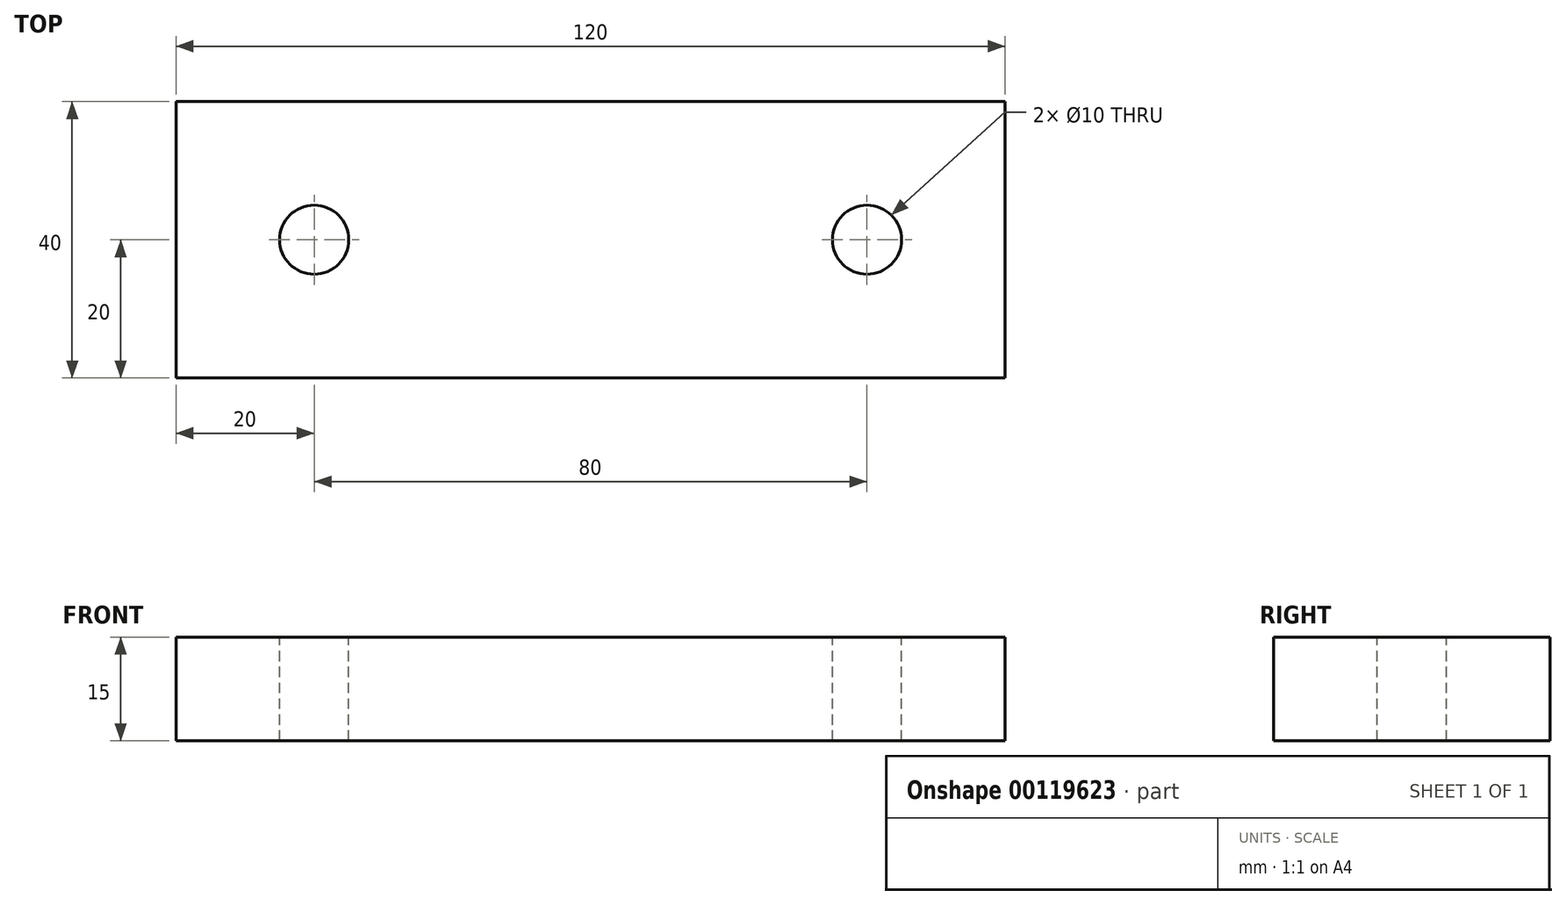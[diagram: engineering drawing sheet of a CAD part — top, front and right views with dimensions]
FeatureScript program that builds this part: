
annotation { "Feature Type Name" : "Feature", "Feature Type Description" : "" }
export const myFeature = defineFeature(function(context is Context, id is Id, definition is map)
    precondition{}
    {
        {
            var Q0;
            Q0=qCreatedBy(makeId("Front.planeOp"),FACE);
            var sketch = newSketch(context, id + "F0", { "sketchPlane" : qUnion([Q0])});
            skLineSegment(sketch, "E0.bottom", {"start": v(0, 0) * mm, "end": v(120, 0) * mm});
            skLineSegment(sketch, "E0.top", {"start": v(0, 15) * mm, "end": v(120, 15) * mm});
            skLineSegment(sketch, "E0.left", {"start": v(0, 0) * mm, "end": v(0, 15) * mm});
            skLineSegment(sketch, "E0.right", {"start": v(120, 0) * mm, "end": v(120, 15) * mm});
            skSolve(sketch);
        }
        {
            var Q0;
            Q0=makeQuery(id+"F0.imprint","IMPRINT",FACE,{"disambiguationData":[TD([[makeQuery(id+"F0.imprint","IMPRINT",EDGE,{"derivedFrom":sQuery(id+"F0.wireOp",EDGE,"E0.bottom")}),1.0]])]});
            extrude(context, id + "F1", {"entities" : qUnion([Q0]), "oppositeDirection" : true, "depth" : 40 * mm});
        }
        {
            var Q0;
            Q0=makeQuery(id+"F1.opExtrude","SWEPT_FACE",FACE,{"disambiguationData":[OSD([sQuery(id+"F0.wireOp",EDGE,"E0.top")])]});
            var sketch = newSketch(context, id + "F2", { "sketchPlane" : qUnion([Q0])});
            skCircle(sketch, "E1", {"center": v(20, 20) * mm, "radius": 5 * mm});
            skCircle(sketch, "E2", {"center": v(100, 20) * mm, "radius": 5 * mm});
            skSolve(sketch);
        }
        {
            var Q0;
            Q0 = qSketchRegion(id + "F2", true);
            extrude(context, id + "F3", {"entities" : qUnion([Q0]), "operationType" : NewBodyOperationType.REMOVE, "endBound" : BoundingType.THROUGH_ALL, "oppositeDirection" : true, "depth" : 25 * mm});
        }
    });
